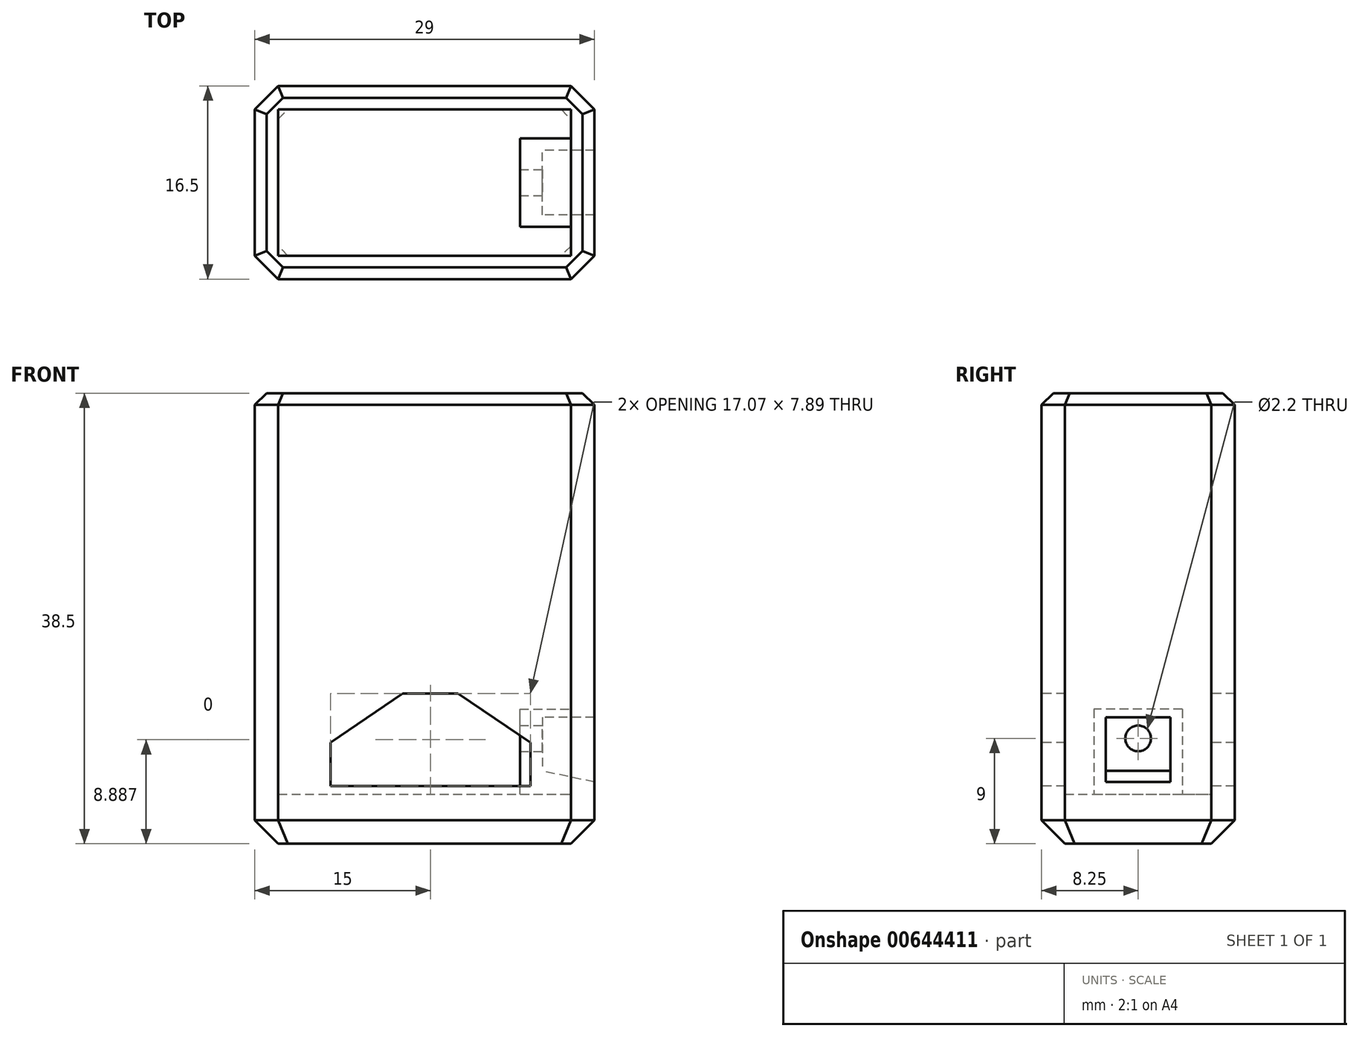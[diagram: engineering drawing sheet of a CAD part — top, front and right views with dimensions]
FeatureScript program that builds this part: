
annotation { "Feature Type Name" : "Feature", "Feature Type Description" : "" }
export const myFeature = defineFeature(function(context is Context, id is Id, definition is map)
    precondition{}
    {
        {
            var Q0;
            Q0=qCreatedBy(makeId("Top.planeOp"),FACE);
            var sketch = newSketch(context, id + "F0", { "sketchPlane" : qUnion([Q0])});
            skLineSegment(sketch, "E0.bottom", {"start": v(0, 0) * mm, "end": v(29, 0) * mm});
            skLineSegment(sketch, "E0.top", {"start": v(0, 16.5) * mm, "end": v(29, 16.5) * mm});
            skLineSegment(sketch, "E0.left", {"start": v(0, 0) * mm, "end": v(0, 16.5) * mm});
            skLineSegment(sketch, "E0.right", {"start": v(29, 0) * mm, "end": v(29, 16.5) * mm});
            skSolve(sketch);
        }
        {
            var Q0;
            Q0=makeQuery(id+"F0.imprint","IMPRINT",FACE,{"disambiguationData":[TD([[makeQuery(id+"F0.imprint","IMPRINT",EDGE,{"derivedFrom":sQuery(id+"F0.wireOp",EDGE,"E0.bottom")}),1.0]])]});
            extrude(context, id + "F1", {"entities" : qUnion([Q0]), "depth" : 38.5 * mm, "offsetDistance" : 25 * mm});
        }
        {
            var Q0;
            Q0=makeQuery(id+"F1.opExtrude","CAP_FACE",FACE,{"disambiguationData":[OSD([sQuery(id+"F0.wireOp",EDGE,"E0.bottom"),sQuery(id+"F0.wireOp",EDGE,"E0.top"),sQuery(id+"F0.wireOp",EDGE,"E0.left"),sQuery(id+"F0.wireOp",EDGE,"E0.right")])],"isStart":false});
            shell(context, id + "F2", {"entities" : qUnion([Q0]), "thickness" : 2 * mm});
        }
        {
            var Q0;
            Q0=makeQuery(id+"F2.opShell","OFFSET_FACE",FACE,{"disambiguationData":[OSD([sQuery(id+"F0.wireOp",EDGE,"E0.bottom"),sQuery(id+"F0.wireOp",EDGE,"E0.top"),sQuery(id+"F0.wireOp",EDGE,"E0.left"),sQuery(id+"F0.wireOp",EDGE,"E0.right")])]});
            extrude(context, id + "F3", {"entities" : qUnion([Q0]), "operationType" : NewBodyOperationType.ADD, "depth" : 2.25 * mm, "offsetDistance" : 25 * mm});
        }
        {
            var Q0;
            Q0=makeQuery(id+"F1.opExtrude","SWEPT_EDGE",EDGE,{"disambiguationData":[OSD([sQuery(id+"F0.wireOp",EDGE,"E0.bottom"),sQuery(id+"F0.wireOp",EDGE,"E0.right")])]});
            var Q1;
            Q1=makeQuery(id+"F1.opExtrude","SWEPT_EDGE",EDGE,{"disambiguationData":[OSD([sQuery(id+"F0.wireOp",EDGE,"E0.top"),sQuery(id+"F0.wireOp",EDGE,"E0.right")])]});
            var Q2;
            Q2=makeQuery(id+"F1.opExtrude","SWEPT_EDGE",EDGE,{"disambiguationData":[OSD([sQuery(id+"F0.wireOp",EDGE,"E0.bottom"),sQuery(id+"F0.wireOp",EDGE,"E0.left")])]});
            var Q3;
            Q3=makeQuery(id+"F1.opExtrude","SWEPT_EDGE",EDGE,{"disambiguationData":[OSD([sQuery(id+"F0.wireOp",EDGE,"E0.top"),sQuery(id+"F0.wireOp",EDGE,"E0.left")])]});
            chamfer(context, id + "F4", {"entities" : qUnion([Q0, Q1, Q2, Q3]), "width" : 2 * mm, "tangentPropagation" : true});
        }
        {
            var Q0;
            Q0=makeQuery(id+"F1.opExtrude","CAP_FACE",FACE,{"disambiguationData":[OSD([sQuery(id+"F0.wireOp",EDGE,"E0.bottom"),sQuery(id+"F0.wireOp",EDGE,"E0.top"),sQuery(id+"F0.wireOp",EDGE,"E0.left"),sQuery(id+"F0.wireOp",EDGE,"E0.right")])],"isStart":true});
            chamfer(context, id + "F5", {"entities" : qUnion([Q0]), "width" : 2 * mm, "tangentPropagation" : true});
        }
        {
            var Q0;
            Q0=makeQuery(id+"F1.opExtrude","CAP_EDGE",EDGE,{"disambiguationData":[OSD([sQuery(id+"F0.wireOp",EDGE,"E0.left")])],"isStart":false});
            var Q1;
            Q1=makeQuery(id+"F1.opExtrude","CAP_EDGE",EDGE,{"disambiguationData":[OSD([sQuery(id+"F0.wireOp",EDGE,"E0.bottom")])],"isStart":false});
            var Q2;
            Q2=makeQuery(id+"F1.opExtrude","CAP_EDGE",EDGE,{"disambiguationData":[OSD([sQuery(id+"F0.wireOp",EDGE,"E0.top")])],"isStart":false});
            var Q3;
            Q3=makeQuery(id+"F1.opExtrude","CAP_EDGE",EDGE,{"disambiguationData":[OSD([sQuery(id+"F0.wireOp",EDGE,"E0.right")])],"isStart":false});
            var Q4;
            {var subQ0=sQuery(id+"F0.wireOp",EDGE,"E0.left");var subQ1=sQuery(id+"F0.wireOp",EDGE,"E0.bottom");Q4=makeQuery(id+"F4.opChamfer","BLEND_EDGE",EDGE,{"blendedFrom":[makeQuery(id+"F1.opExtrude","SWEPT_EDGE",EDGE,{"disambiguationData":[OSD([subQ1,subQ0])]}),makeQuery(id+"F1.opExtrude","CAP_FACE",FACE,{"disambiguationData":[OSD([subQ1,sQuery(id+"F0.wireOp",EDGE,"E0.top"),subQ0,sQuery(id+"F0.wireOp",EDGE,"E0.right")])],"isStart":false})],"blendedInto":[makeQuery(id+"F1.opExtrude","CAP_FACE",FACE,{"disambiguationData":[OSD([subQ1,sQuery(id+"F0.wireOp",EDGE,"E0.top"),subQ0,sQuery(id+"F0.wireOp",EDGE,"E0.right")])],"isStart":false})]});}
            var Q5;
            {var subQ0=sQuery(id+"F0.wireOp",EDGE,"E0.right");var subQ1=sQuery(id+"F0.wireOp",EDGE,"E0.top");Q5=makeQuery(id+"F4.opChamfer","BLEND_EDGE",EDGE,{"blendedFrom":[makeQuery(id+"F1.opExtrude","SWEPT_EDGE",EDGE,{"disambiguationData":[OSD([subQ1,subQ0])]}),makeQuery(id+"F1.opExtrude","CAP_FACE",FACE,{"disambiguationData":[OSD([sQuery(id+"F0.wireOp",EDGE,"E0.bottom"),subQ1,sQuery(id+"F0.wireOp",EDGE,"E0.left"),subQ0])],"isStart":false})],"blendedInto":[makeQuery(id+"F1.opExtrude","CAP_FACE",FACE,{"disambiguationData":[OSD([sQuery(id+"F0.wireOp",EDGE,"E0.bottom"),subQ1,sQuery(id+"F0.wireOp",EDGE,"E0.left"),subQ0])],"isStart":false})]});}
            var Q6;
            {var subQ0=sQuery(id+"F0.wireOp",EDGE,"E0.left");var subQ1=sQuery(id+"F0.wireOp",EDGE,"E0.top");Q6=makeQuery(id+"F4.opChamfer","BLEND_EDGE",EDGE,{"blendedFrom":[makeQuery(id+"F1.opExtrude","SWEPT_EDGE",EDGE,{"disambiguationData":[OSD([subQ1,subQ0])]}),makeQuery(id+"F1.opExtrude","CAP_FACE",FACE,{"disambiguationData":[OSD([sQuery(id+"F0.wireOp",EDGE,"E0.bottom"),subQ1,subQ0,sQuery(id+"F0.wireOp",EDGE,"E0.right")])],"isStart":false})],"blendedInto":[makeQuery(id+"F1.opExtrude","CAP_FACE",FACE,{"disambiguationData":[OSD([sQuery(id+"F0.wireOp",EDGE,"E0.bottom"),subQ1,subQ0,sQuery(id+"F0.wireOp",EDGE,"E0.right")])],"isStart":false})]});}
            var Q7;
            {var subQ0=sQuery(id+"F0.wireOp",EDGE,"E0.right");var subQ1=sQuery(id+"F0.wireOp",EDGE,"E0.bottom");Q7=makeQuery(id+"F4.opChamfer","BLEND_EDGE",EDGE,{"blendedFrom":[makeQuery(id+"F1.opExtrude","SWEPT_EDGE",EDGE,{"disambiguationData":[OSD([subQ1,subQ0])]}),makeQuery(id+"F1.opExtrude","CAP_FACE",FACE,{"disambiguationData":[OSD([subQ1,sQuery(id+"F0.wireOp",EDGE,"E0.top"),sQuery(id+"F0.wireOp",EDGE,"E0.left"),subQ0])],"isStart":false})],"blendedInto":[makeQuery(id+"F1.opExtrude","CAP_FACE",FACE,{"disambiguationData":[OSD([subQ1,sQuery(id+"F0.wireOp",EDGE,"E0.top"),sQuery(id+"F0.wireOp",EDGE,"E0.left"),subQ0])],"isStart":false})]});}
            chamfer(context, id + "F6", {"entities" : qUnion([Q0, Q1, Q2, Q3, Q4, Q5, Q6, Q7]), "width" : 1 * mm, "tangentPropagation" : true});
        }
        {
            var Q0;
            Q0=makeQuery(id+"F1.opExtrude","SWEPT_FACE",FACE,{"disambiguationData":[OSD([sQuery(id+"F0.wireOp",EDGE,"E0.bottom")])]});
            var sketch = newSketch(context, id + "F7", { "sketchPlane" : qUnion([Q0])});
            skLineSegment(sketch, "E1", {"start": v(12.63, 12.83) * mm, "end": v(17.36, 12.83) * mm});
            skLineSegment(sketch, "E2", {"start": v(17.36, 12.83) * mm, "end": v(23.54, 8.66) * mm});
            skLineSegment(sketch, "E3", {"start": v(23.54, 8.66) * mm, "end": v(23.54, 4.94) * mm});
            skLineSegment(sketch, "E4", {"start": v(23.54, 4.94) * mm, "end": v(6.46, 4.94) * mm});
            skLineSegment(sketch, "E5", {"start": v(6.46, 4.94) * mm, "end": v(6.46, 8.66) * mm});
            skLineSegment(sketch, "E6", {"start": v(6.46, 8.66) * mm, "end": v(12.64, 12.83) * mm});
            skSolve(sketch);
        }
        {
            var Q0;
            Q0=makeQuery(id+"F7.imprint","IMPRINT",FACE,{"disambiguationData":[TD([[makeQuery(id+"F7.imprint","IMPRINT",EDGE,{"derivedFrom":sQuery(id+"F7.wireOp",EDGE,"E1")}),-1.0]])]});
            extrude(context, id + "F8", {"entities" : qUnion([Q0]), "operationType" : NewBodyOperationType.REMOVE, "endBound" : BoundingType.THROUGH_ALL, "oppositeDirection" : true, "depth" : 25 * mm, "offsetDistance" : 25 * mm});
        }
        {
            var Q0;
            Q0=makeQuery(id+"F1.opExtrude","SWEPT_FACE",FACE,{"disambiguationData":[OSD([sQuery(id+"F0.wireOp",EDGE,"E0.right")])]});
            var sketch = newSketch(context, id + "F9", { "sketchPlane" : qUnion([Q0])});
            skLineSegment(sketch, "E7.bottom", {"start": v(4.48, 4.25) * mm, "end": v(12.02, 4.25) * mm});
            skLineSegment(sketch, "E7.top", {"start": v(4.48, 11.5) * mm, "end": v(12.02, 11.5) * mm});
            skLineSegment(sketch, "E7.left", {"start": v(4.48, 4.25) * mm, "end": v(4.48, 11.5) * mm});
            skLineSegment(sketch, "E7.right", {"start": v(12.02, 4.25) * mm, "end": v(12.02, 11.5) * mm});
            skCircle(sketch, "E8", {"center": v(8.25, 9) * mm, "radius": 1.1 * mm});
            skPoint(sketch, "E9", {"position": v(8.25, 11.5) * mm});
            skSolve(sketch);
        }
        {
            var Q0;
            Q0=makeQuery(id+"F9.imprint","IMPRINT",FACE,{"disambiguationData":[TD([[makeQuery(id+"F9.imprint","IMPRINT",EDGE,{"derivedFrom":sQuery(id+"F9.wireOp",EDGE,"E7.bottom")}),1.0]])]});
            extrude(context, id + "F10", {"entities" : qUnion([Q0]), "operationType" : NewBodyOperationType.ADD, "oppositeDirection" : true, "depth" : 6.35 * mm, "offsetDistance" : 25 * mm});
        }
        {
            var Q0;
            Q0=makeQuery(id+"F1.opExtrude","SWEPT_FACE",FACE,{"disambiguationData":[OSD([sQuery(id+"F0.wireOp",EDGE,"E0.right")])]});
            var sketch = newSketch(context, id + "F11", { "sketchPlane" : qUnion([Q0])});
            skLineSegment(sketch, "E10.bottom", {"start": v(5.48, 10.8) * mm, "end": v(11.02, 10.8) * mm});
            skLineSegment(sketch, "E10.top", {"start": v(5.48, 5.27) * mm, "end": v(11.02, 5.27) * mm});
            skLineSegment(sketch, "E10.left", {"start": v(5.48, 10.8) * mm, "end": v(5.48, 5.27) * mm});
            skLineSegment(sketch, "E10.right", {"start": v(11.02, 10.8) * mm, "end": v(11.02, 5.27) * mm});
            skSolve(sketch);
        }
        {
            var Q0;
            Q0=makeQuery(id+"F11.imprint","IMPRINT",FACE,{"disambiguationData":[TD([[makeQuery(id+"F11.imprint","IMPRINT",EDGE,{"derivedFrom":sQuery(id+"F11.wireOp",EDGE,"E10.bottom")}),1.0]])]});
            cPlane(context, id + "F12", {"entities" : qUnion([Q0]), "cplaneType" : CPlaneType.OFFSET, "offset" : 4.45 * mm, "oppositeDirection" : true, "width" : 150 * mm, "height" : 150 * mm});
        }
        {
            var Q0;
            Q0=qCreatedBy(id+"F12.planeOp",FACE);
            var sketch = newSketch(context, id + "F13", { "sketchPlane" : qUnion([Q0])});
            skLineSegment(sketch, "E11.bottom", {"start": v(5.48, 10.8) * mm, "end": v(11.02, 10.8) * mm});
            skLineSegment(sketch, "E11.top", {"start": v(5.48, 6.22) * mm, "end": v(11.02, 6.22) * mm});
            skLineSegment(sketch, "E11.left", {"start": v(5.48, 10.8) * mm, "end": v(5.48, 6.22) * mm});
            skLineSegment(sketch, "E11.right", {"start": v(11.02, 10.8) * mm, "end": v(11.02, 6.22) * mm});
            skSolve(sketch);
        }
        {
            var Q1;
            Q1 = qSketchRegion(id + "F11", true);
            var Q2;
            Q2 = qSketchRegion(id + "F13", true);
            loft(context, id + "F14", {"operationType" : NewBodyOperationType.REMOVE, "sheetProfilesArray" : [{ "sheetProfileEntities" : qUnion([Q1]) }, { "sheetProfileEntities" : qUnion([Q2]) }]});
        }
    });
